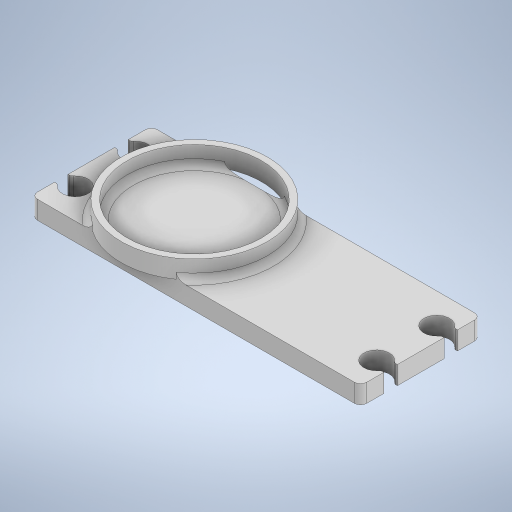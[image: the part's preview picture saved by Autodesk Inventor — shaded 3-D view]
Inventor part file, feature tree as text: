
AUTODESK INVENTOR PART (.ipt)
format: ipt  version: 2024 (Build 280153000, 153)  size: 352,768 bytes
history: native  units: mm
features: other x5, reference x4, extrude x2, fillet x2, sketch x2, plane x1
ambient origin geometry x8: Origin, YZ Plane, XZ Plane, XY Plane, X Axis, Y Axis, Z Axis, Center Point
bodies: Solid1 (feature_tree)
feature tree (16):
  extrude  "Extrusion1"  Depth=1.0mm
  plane  "Work Plane1"
  extrude  "Extrusion2"  Depth=1.0mm TaperAngle=0.0deg
  fillet  "Fillet1"  Radius=1.0mm
  fillet  "Fillet2"  Radius=1.0mm
  sketch  "Sketch1"  dims[d0=24.0mm d1=1.0mm]
  reference  "Reference1"
  reference  "Reference2"
  sketch  "Sketch2"  dims[d2=3.0mm d3=0.0mm d4=3.0mm d5=0.0mm d6=1.0mm d7=1.0mm]
  reference  "Reference3"
  reference  "Reference4"
  other  "<userpath> windows\Documents\Inventor\Robotska_roka\roka.iam"
  other  "roka.iam"
  other  "Servo Motor MG996R  With Attachments:7"
  other  "servoMotorMG996R_7"
  other  "servoMotorMG996R_6"
